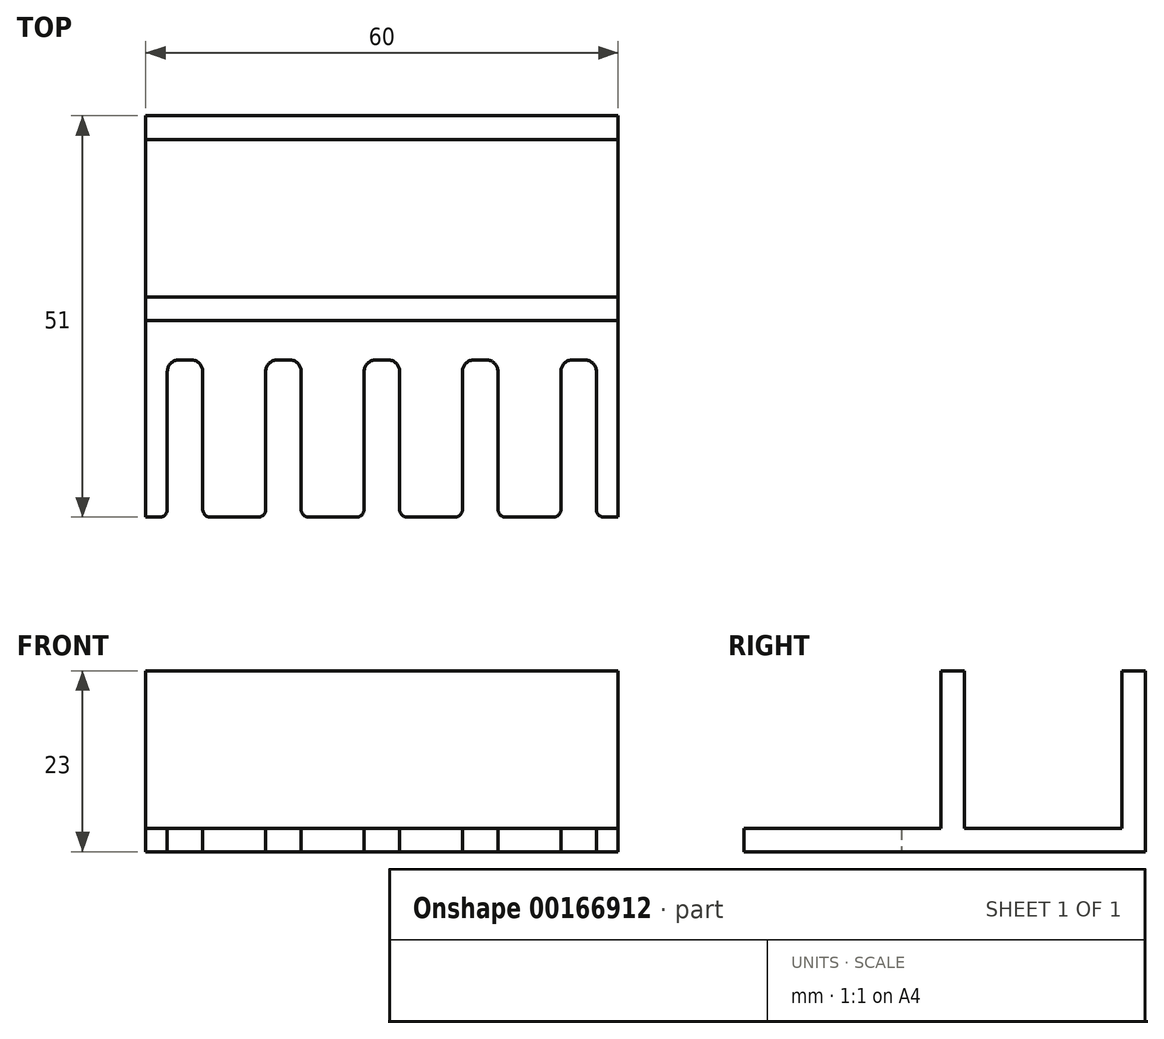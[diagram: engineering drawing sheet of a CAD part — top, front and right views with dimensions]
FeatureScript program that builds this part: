
annotation { "Feature Type Name" : "Feature", "Feature Type Description" : "" }
export const myFeature = defineFeature(function(context is Context, id is Id, definition is map)
    precondition{}
    {
        {
            var Q0;
            Q0=qCreatedBy(makeId("Top.planeOp"),FACE);
            var sketch = newSketch(context, id + "F0", { "sketchPlane" : qUnion([Q0])});
            skLineSegment(sketch, "E0.bottom", {"start": v(-30, 13) * mm, "end": v(30, 13) * mm});
            skLineSegment(sketch, "E0.top", {"start": v(-30, -13) * mm, "end": v(30, -13) * mm});
            skLineSegment(sketch, "E0.left", {"start": v(-30, 13) * mm, "end": v(-30, -13) * mm});
            skLineSegment(sketch, "E0.right", {"start": v(30, 13) * mm, "end": v(30, -13) * mm});
            skPoint(sketch, "E0.middle", {"position": v(0, 0) * mm});
            skLineSegment(sketch, "E1", {"start": v(-30, -13) * mm, "end": v(-30, -38) * mm});
            skLineSegment(sketch, "E2", {"start": v(30, -13) * mm, "end": v(30, -38) * mm});
            skLineSegment(sketch, "E3", {"start": v(-30, -38) * mm, "end": v(-28.25, -38) * mm});
            skLineSegment(sketch, "E4", {"start": v(-27.25, -37) * mm, "end": v(-27.25, -19.5) * mm});
            skLineSegment(sketch, "E5", {"start": v(-25.75, -18) * mm, "end": v(-24.25, -18) * mm});
            skLineSegment(sketch, "E6", {"start": v(-22.75, -19.5) * mm, "end": v(-22.75, -37) * mm});
            skLineSegment(sketch, "E7", {"start": v(-21.75, -38) * mm, "end": v(-18.75, -38) * mm});
            skPoint(sketch, "E8.visualSharp", {"position": v(-27.25, -38) * mm});
            skArc(sketch, "E8.filletArc", {"start": v(-28.25, -38) * mm, "mid": v(-27.54, -37.7) * mm, "end": v(-27.25, -37) * mm});
            skPoint(sketch, "E9.visualSharp", {"position": v(-22.75, -38) * mm});
            skArc(sketch, "E9.filletArc", {"start": v(-22.75, -37) * mm, "mid": v(-22.46, -37.7) * mm, "end": v(-21.75, -38) * mm});
            skPoint(sketch, "E10.visualSharp", {"position": v(-27.25, -18) * mm});
            skArc(sketch, "E10.filletArc", {"start": v(-25.75, -18) * mm, "mid": v(-26.81, -18.44) * mm, "end": v(-27.25, -19.5) * mm});
            skPoint(sketch, "E11.visualSharp", {"position": v(-22.75, -18) * mm});
            skArc(sketch, "E11.filletArc", {"start": v(-22.75, -19.5) * mm, "mid": v(-23.19, -18.44) * mm, "end": v(-24.25, -18) * mm});
            skLineSegment(sketch, "E12", {"start": v(-18.75, -38) * mm, "end": v(-15.75, -38) * mm});
            skLineSegment(sketch, "E13", {"start": v(-14.75, -37) * mm, "end": v(-14.75, -19.5) * mm});
            skLineSegment(sketch, "E14", {"start": v(-13.25, -18) * mm, "end": v(-11.75, -18) * mm});
            skLineSegment(sketch, "E15", {"start": v(-10.25, -19.5) * mm, "end": v(-10.25, -37) * mm});
            skLineSegment(sketch, "E16", {"start": v(-9.25, -38) * mm, "end": v(-3.25, -38) * mm});
            skLineSegment(sketch, "E17", {"start": v(-2.25, -37) * mm, "end": v(-2.25, -19.5) * mm});
            skLineSegment(sketch, "E18", {"start": v(-0.75, -18) * mm, "end": v(0.75, -18) * mm});
            skLineSegment(sketch, "E19", {"start": v(2.25, -19.5) * mm, "end": v(2.25, -37) * mm});
            skLineSegment(sketch, "E20", {"start": v(3.25, -38) * mm, "end": v(9.25, -38) * mm});
            skLineSegment(sketch, "E21", {"start": v(10.25, -37) * mm, "end": v(10.25, -19.5) * mm});
            skLineSegment(sketch, "E22", {"start": v(11.75, -18) * mm, "end": v(13.25, -18) * mm});
            skLineSegment(sketch, "E23", {"start": v(14.75, -19.5) * mm, "end": v(14.75, -37) * mm});
            skLineSegment(sketch, "E24", {"start": v(15.75, -38) * mm, "end": v(21.75, -38) * mm});
            skLineSegment(sketch, "E25", {"start": v(22.75, -37) * mm, "end": v(22.75, -19.5) * mm});
            skLineSegment(sketch, "E26", {"start": v(24.25, -18) * mm, "end": v(25.75, -18) * mm});
            skLineSegment(sketch, "E27", {"start": v(27.25, -19.5) * mm, "end": v(27.25, -37) * mm});
            skLineSegment(sketch, "E28", {"start": v(28.25, -38) * mm, "end": v(30, -38) * mm});
            skPoint(sketch, "E29.visualSharp", {"position": v(-14.75, -38) * mm});
            skArc(sketch, "E29.filletArc", {"start": v(-15.75, -38) * mm, "mid": v(-15.04, -37.7) * mm, "end": v(-14.75, -37) * mm});
            skPoint(sketch, "E30.visualSharp", {"position": v(-10.25, -38) * mm});
            skArc(sketch, "E30.filletArc", {"start": v(-10.25, -37) * mm, "mid": v(-9.96, -37.7) * mm, "end": v(-9.25, -38) * mm});
            skPoint(sketch, "E31.visualSharp", {"position": v(-2.25, -38) * mm});
            skArc(sketch, "E31.filletArc", {"start": v(-3.25, -38) * mm, "mid": v(-2.54, -37.7) * mm, "end": v(-2.25, -37) * mm});
            skPoint(sketch, "E32.visualSharp", {"position": v(2.25, -38) * mm});
            skArc(sketch, "E32.filletArc", {"start": v(2.25, -37) * mm, "mid": v(2.54, -37.7) * mm, "end": v(3.25, -38) * mm});
            skPoint(sketch, "E33.visualSharp", {"position": v(10.25, -38) * mm});
            skArc(sketch, "E33.filletArc", {"start": v(9.25, -38) * mm, "mid": v(9.96, -37.7) * mm, "end": v(10.25, -37) * mm});
            skPoint(sketch, "E34.visualSharp", {"position": v(14.75, -38) * mm});
            skArc(sketch, "E34.filletArc", {"start": v(14.75, -37) * mm, "mid": v(15.04, -37.7) * mm, "end": v(15.75, -38) * mm});
            skPoint(sketch, "E35.visualSharp", {"position": v(22.75, -38) * mm});
            skArc(sketch, "E35.filletArc", {"start": v(21.75, -38) * mm, "mid": v(22.46, -37.7) * mm, "end": v(22.75, -37) * mm});
            skPoint(sketch, "E36.visualSharp", {"position": v(27.25, -38) * mm});
            skArc(sketch, "E36.filletArc", {"start": v(27.25, -37) * mm, "mid": v(27.54, -37.7) * mm, "end": v(28.25, -38) * mm});
            skPoint(sketch, "E37.visualSharp", {"position": v(-14.75, -18) * mm});
            skArc(sketch, "E37.filletArc", {"start": v(-13.25, -18) * mm, "mid": v(-14.31, -18.44) * mm, "end": v(-14.75, -19.5) * mm});
            skPoint(sketch, "E38.visualSharp", {"position": v(-10.25, -18) * mm});
            skArc(sketch, "E38.filletArc", {"start": v(-10.25, -19.5) * mm, "mid": v(-10.69, -18.44) * mm, "end": v(-11.75, -18) * mm});
            skPoint(sketch, "E39.visualSharp", {"position": v(-2.25, -18) * mm});
            skArc(sketch, "E39.filletArc", {"start": v(-0.75, -18) * mm, "mid": v(-1.81, -18.44) * mm, "end": v(-2.25, -19.5) * mm});
            skPoint(sketch, "E40.visualSharp", {"position": v(2.25, -18) * mm});
            skArc(sketch, "E40.filletArc", {"start": v(2.25, -19.5) * mm, "mid": v(1.81, -18.44) * mm, "end": v(0.75, -18) * mm});
            skPoint(sketch, "E41.visualSharp", {"position": v(10.25, -18) * mm});
            skArc(sketch, "E41.filletArc", {"start": v(11.75, -18) * mm, "mid": v(10.69, -18.44) * mm, "end": v(10.25, -19.5) * mm});
            skPoint(sketch, "E42.visualSharp", {"position": v(14.75, -18) * mm});
            skArc(sketch, "E42.filletArc", {"start": v(14.75, -19.5) * mm, "mid": v(14.31, -18.44) * mm, "end": v(13.25, -18) * mm});
            skPoint(sketch, "E43.visualSharp", {"position": v(22.75, -18) * mm});
            skArc(sketch, "E43.filletArc", {"start": v(24.25, -18) * mm, "mid": v(23.19, -18.44) * mm, "end": v(22.75, -19.5) * mm});
            skPoint(sketch, "E44.visualSharp", {"position": v(27.25, -18) * mm});
            skArc(sketch, "E44.filletArc", {"start": v(27.25, -19.5) * mm, "mid": v(26.81, -18.44) * mm, "end": v(25.75, -18) * mm});
            skSolve(sketch);
        }
        {
            var Q0;
            Q0=makeQuery(id+"F0.imprint","IMPRINT",FACE,{"disambiguationData":[TD([[makeQuery(id+"F0.imprint","IMPRINT",EDGE,{"derivedFrom":sQuery(id+"F0.wireOp",EDGE,"E0.bottom")}),-1.0]])]});
            var Q1;
            Q1=makeQuery(id+"F0.imprint","IMPRINT",FACE,{"disambiguationData":[TD([[makeQuery(id+"F0.imprint","IMPRINT",EDGE,{"derivedFrom":sQuery(id+"F0.wireOp",EDGE,"E0.top")}),-1.0]])]});
            extrude(context, id + "F1", {"entities" : qUnion([Q0, Q1]), "depth" : 3 * mm});
        }
        {
            var Q0;
            Q0=makeQuery(id+"F1.opExtrude","CAP_FACE",FACE,{"disambiguationData":[OSD([sQuery(id+"F0.wireOp",EDGE,"E0.bottom"),sQuery(id+"F0.wireOp",EDGE,"E0.left"),sQuery(id+"F0.wireOp",EDGE,"E0.right"),sQuery(id+"F0.wireOp",EDGE,"E1"),sQuery(id+"F0.wireOp",EDGE,"LC4PGwtC-cwF6-hu4u-gilk-vYaeQbCKIp22"),sQuery(id+"F0.wireOp",EDGE,"VCmP6TtW-RcqL-YGeu-Tidw-IUAYdoSxl4k9"),sQuery(id+"F0.wireOp",EDGE,"xt8EVL6S-lyoH-nvkE-7s2k-m5lgjWmenGVK"),sQuery(id+"F0.wireOp",EDGE,"HaTm7lg3-vY9K-Tcgu-CsRM-wYIfSgVVkeDh"),sQuery(id+"F0.wireOp",EDGE,"twx1IIYy-rddA-xoBU-Vwtc-AuTk3Q1ymrhz"),sQuery(id+"F0.wireOp",EDGE,"a6441634-3664-49ab-9861-bddf5f363dea.filletArc"),sQuery(id+"F0.wireOp",EDGE,"c3abe9f2-a1a6-4466-8204-f58448fca995.filletArc"),sQuery(id+"F0.wireOp",EDGE,"ece09503-428c-4b5f-95a0-5d05a5e4997c.filletArc"),sQuery(id+"F0.wireOp",EDGE,"pouCUyZR-bWe1-r5r6-HkmU-Zea7mCywnLQb"),sQuery(id+"F0.wireOp",EDGE,"kzDzAVgN-Yg4L-YtN1-vTa9-H6SGxtV0WUrI"),sQuery(id+"F0.wireOp",EDGE,"453222cc-61eb-4c05-a2c6-d9c0fb1048a3.filletArc"),sQuery(id+"F0.wireOp",EDGE,"b03b8217-88be-4c4b-adde-c325bcf08f2d.filletArc"),sQuery(id+"F0.wireOp",EDGE,"a5c0ca57-d54c-403e-b413-19259bc8d4d2.filletArc"),sQuery(id+"F0.wireOp",EDGE,"mDVW3tj2-7yW4-ynUi-ITTL-NP6ZAPG7X3sE"),sQuery(id+"F0.wireOp",EDGE,"UYcOpEr8-DjVf-iyd2-6C9c-ozSDlcg9zkZO"),sQuery(id+"F0.wireOp",EDGE,"K46FuZtp-MVH5-KAaZ-iSRX-JxPPexCgMWBL"),sQuery(id+"F0.wireOp",EDGE,"cb7ed820-062a-4bd6-bb46-d2bf007885b7.filletArc"),sQuery(id+"F0.wireOp",EDGE,"e60bf902-7c87-435b-a8b2-c1d7c5083184.filletArc"),sQuery(id+"F0.wireOp",EDGE,"cd1dc894-9c82-4d8b-8d6a-67e5ceed5467.filletArc"),sQuery(id+"F0.wireOp",EDGE,"738753c9-5b85-44d1-92f4-44b73e7c3188.trimOffspring"),sQuery(id+"F0.wireOp",EDGE,"d8585476-6f32-46cc-a35b-d7b37d6d7cb3.trimOffspring"),sQuery(id+"F0.wireOp",EDGE,"vplBzqFt-PoNN-IEKJ-k4i0-oUoxCMhFI8nO")])],"isStart":false});
            var sketch = newSketch(context, id + "F2", { "sketchPlane" : qUnion([Q0])});
            skLineSegment(sketch, "E45", {"start": v(-30, 13) * mm, "end": v(-30, 10) * mm});
            skLineSegment(sketch, "E46", {"start": v(-30, 10) * mm, "end": v(30, 10) * mm});
            skLineSegment(sketch, "E47", {"start": v(30, 10) * mm, "end": v(30, 13) * mm});
            skSolve(sketch);
        }
        {
            var Q0;
            Q0=makeQuery(id+"F2.imprint","IMPRINT",FACE,{"disambiguationData":[TD([[makeQuery(id+"F2.imprint","IMPRINT",EDGE,{"derivedFrom":sQuery(id+"F2.wireOp",EDGE,"E45")}),1.0]])]});
            extrude(context, id + "F3", {"entities" : qUnion([Q0]), "operationType" : NewBodyOperationType.ADD, "depth" : 20 * mm});
        }
        {
            var Q0;
            Q0=makeQuery(id+"F1.opExtrude","CAP_FACE",FACE,{"disambiguationData":[OSD([sQuery(id+"F0.wireOp",EDGE,"E0.bottom"),sQuery(id+"F0.wireOp",EDGE,"E0.left"),sQuery(id+"F0.wireOp",EDGE,"E0.right"),sQuery(id+"F0.wireOp",EDGE,"E1"),sQuery(id+"F0.wireOp",EDGE,"LC4PGwtC-cwF6-hu4u-gilk-vYaeQbCKIp22"),sQuery(id+"F0.wireOp",EDGE,"VCmP6TtW-RcqL-YGeu-Tidw-IUAYdoSxl4k9"),sQuery(id+"F0.wireOp",EDGE,"xt8EVL6S-lyoH-nvkE-7s2k-m5lgjWmenGVK"),sQuery(id+"F0.wireOp",EDGE,"HaTm7lg3-vY9K-Tcgu-CsRM-wYIfSgVVkeDh"),sQuery(id+"F0.wireOp",EDGE,"twx1IIYy-rddA-xoBU-Vwtc-AuTk3Q1ymrhz"),sQuery(id+"F0.wireOp",EDGE,"a6441634-3664-49ab-9861-bddf5f363dea.filletArc"),sQuery(id+"F0.wireOp",EDGE,"c3abe9f2-a1a6-4466-8204-f58448fca995.filletArc"),sQuery(id+"F0.wireOp",EDGE,"ece09503-428c-4b5f-95a0-5d05a5e4997c.filletArc"),sQuery(id+"F0.wireOp",EDGE,"pouCUyZR-bWe1-r5r6-HkmU-Zea7mCywnLQb"),sQuery(id+"F0.wireOp",EDGE,"kzDzAVgN-Yg4L-YtN1-vTa9-H6SGxtV0WUrI"),sQuery(id+"F0.wireOp",EDGE,"453222cc-61eb-4c05-a2c6-d9c0fb1048a3.filletArc"),sQuery(id+"F0.wireOp",EDGE,"b03b8217-88be-4c4b-adde-c325bcf08f2d.filletArc"),sQuery(id+"F0.wireOp",EDGE,"a5c0ca57-d54c-403e-b413-19259bc8d4d2.filletArc"),sQuery(id+"F0.wireOp",EDGE,"mDVW3tj2-7yW4-ynUi-ITTL-NP6ZAPG7X3sE"),sQuery(id+"F0.wireOp",EDGE,"UYcOpEr8-DjVf-iyd2-6C9c-ozSDlcg9zkZO"),sQuery(id+"F0.wireOp",EDGE,"K46FuZtp-MVH5-KAaZ-iSRX-JxPPexCgMWBL"),sQuery(id+"F0.wireOp",EDGE,"cb7ed820-062a-4bd6-bb46-d2bf007885b7.filletArc"),sQuery(id+"F0.wireOp",EDGE,"e60bf902-7c87-435b-a8b2-c1d7c5083184.filletArc"),sQuery(id+"F0.wireOp",EDGE,"cd1dc894-9c82-4d8b-8d6a-67e5ceed5467.filletArc"),sQuery(id+"F0.wireOp",EDGE,"738753c9-5b85-44d1-92f4-44b73e7c3188.trimOffspring"),sQuery(id+"F0.wireOp",EDGE,"d8585476-6f32-46cc-a35b-d7b37d6d7cb3.trimOffspring"),sQuery(id+"F0.wireOp",EDGE,"vplBzqFt-PoNN-IEKJ-k4i0-oUoxCMhFI8nO")])],"isStart":false});
            var sketch = newSketch(context, id + "F4", { "sketchPlane" : qUnion([Q0])});
            skLineSegment(sketch, "E48", {"start": v(-30, -10) * mm, "end": v(30, -10) * mm});
            skLineSegment(sketch, "E49", {"start": v(-30, -10) * mm, "end": v(-30, -13) * mm});
            skLineSegment(sketch, "E50", {"start": v(-30, -13) * mm, "end": v(30, -13) * mm});
            skSolve(sketch);
        }
        {
            var Q0;
            {var subQ0=sQuery(id+"F4.wireOp",EDGE,"E48");Q0=makeQuery(id+"F4.imprint","IMPRINT",FACE,{"disambiguationData":[TD([[makeQuery(id+"F4.imprint","IMPRINT",EDGE,{"derivedFrom":subQ0}),-1.0]])]});}
            extrude(context, id + "F5", {"entities" : qUnion([Q0]), "operationType" : NewBodyOperationType.ADD, "depth" : 20 * mm});
        }
    });
